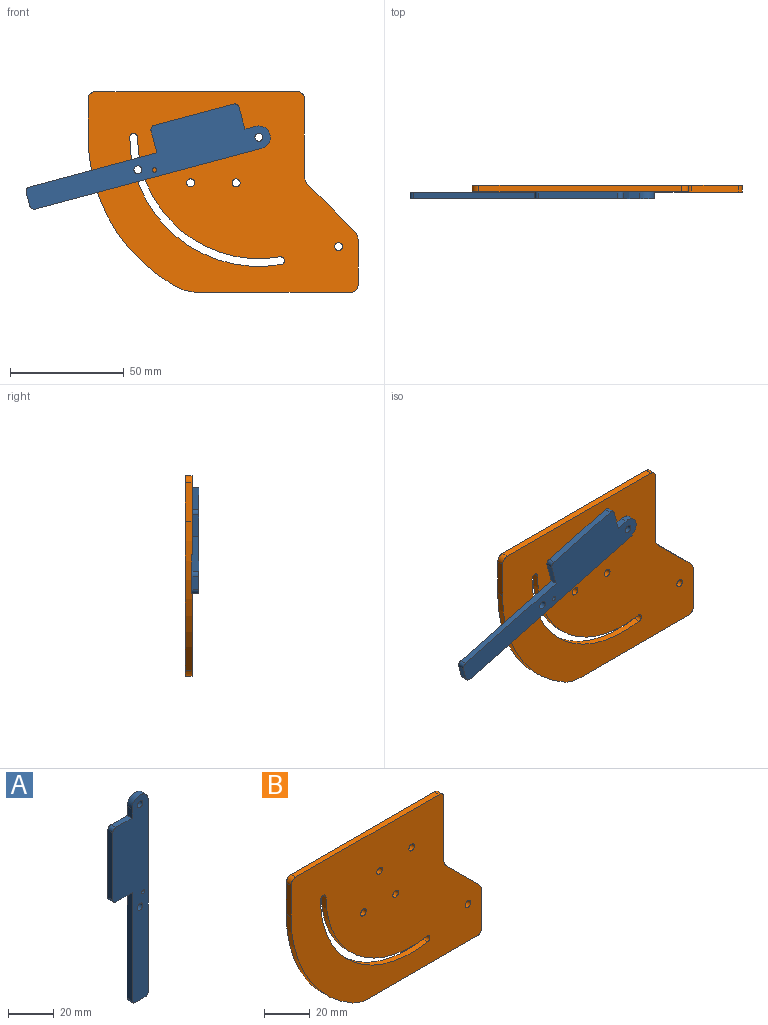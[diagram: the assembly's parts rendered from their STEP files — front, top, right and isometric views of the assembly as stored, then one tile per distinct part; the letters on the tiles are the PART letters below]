
ASSEMBLY  parts=2 mates=1
PART A: 17 faces, bbox 22x3x110 mm
  f0: cylinder r=2mm len=3mm, axis (0,1,0), area 9.4mm2, adj f1,f14,f15,f16
  f1: plane 6x3mm, normal (0,0,-1), area 18mm2, adj f0,f2,f15,f16
  f2: cylinder r=2mm len=3mm, axis (0,1,0), area 9.4mm2, adj f1,f3,f15,f16
  f3: plane 103x3mm, normal (1,0,0), area 309mm2, adj f2,f4,f15,f16
  f4: cylinder r=5mm len=10mm, axis (0,1,0), area 47.1mm2, adj f3,f5,f15,f16
  f5: plane 5x3mm, normal (-1,0,0), area 15mm2, adj f4,f6,f15,f16
  f6: plane 10x3mm, normal (0,0,1), area 30mm2, adj f5,f7,f15,f16
  f7: cylinder r=2mm len=3mm, axis (0,1,0), area 9.4mm2, adj f6,f8,f15,f16
  f8: plane 36x3mm, normal (-1,0,0), area 108mm2, adj f7,f9,f15,f16
  f9: cylinder r=2mm len=3mm, axis (0,1,0), area 9.4mm2, adj f8,f10,f15,f16
  f10: plane 10x3mm, normal (0,0,-1), area 30mm2, adj f9,f14,f15,f16
  f11: cylinder r=1.75mm len=3.5mm, axis (0,1,0), area 33mm2, adj f15,f16
  f12: cylinder r=1.75mm len=3.5mm, axis (0,1,0), area 33mm2, adj f15,f16
  f13: cylinder r=1mm len=3mm, axis (0,1,0), area 18.8mm2, adj f15,f16
  f14: plane 58x3mm, normal (-1,0,0), area 174mm2, adj f0,f10,f15,f16
  f15: plane 110x22mm, normal (0,-1,0), area 1543.5mm2, adj f0,f1,f2,f3,f4,f5,f6,f7
  f16: plane 110x22mm, normal (0,1,0), area 1543.5mm2, adj f0,f1,f2,f3,f4,f5,f6,f7
PART B: 24 faces, bbox 118.5x3x88 mm
  f0: plane 34.17x3mm, normal (1,0,0), area 102.5mm2, adj f1,f21,f22,f23
  f1: cylinder r=3mm len=3mm, axis (0,1,0), area 14.1mm2, adj f0,f2,f22,f23
  f2: plane 89x3mm, normal (0,0,1), area 267mm2, adj f1,f3,f22,f23
  f3: cylinder r=3mm len=3mm, axis (0,1,0), area 14.1mm2, adj f2,f4,f22,f23
  f4: plane 17x3mm, normal (-1,0,0), area 51mm2, adj f3,f5,f22,f23
  f5: cylinder r=75mm len=65.45mm, axis (0,1,0), area 238.7mm2, adj f4,f6,f22,f23
  f6: cylinder r=20mm len=9.76mm, axis (0,1,0), area 30.6mm2, adj f5,f7,f22,f23
  f7: plane 67.36x3mm, normal (0,0,-1), area 202.1mm2, adj f6,f8,f22,f23
  f8: cylinder r=3mm len=3mm, axis (0,1,0), area 14.1mm2, adj f7,f9,f22,f23
  f9: plane 20.18x3mm, normal (1,0,0), area 60.5mm2, adj f8,f10,f22,f23
  f10: cylinder r=5mm len=3.54mm, axis (0,1,0), area 11.8mm2, adj f9,f11,f22,f23
  f11: plane 20.58x20.58mm, normal (0.71,0,0.71), area 87.3mm2, adj f10,f21,f22,f23
  f12: cylinder r=1.7mm len=3.4mm, axis (0,1,0), area 16mm2, adj f13,f20,f22,f23
  f13: cylinder r=53.3mm len=62.56mm, axis (0,1,0), area 279.1mm2, adj f12,f14,f22,f23
  f14: cylinder r=1.7mm len=3.37mm, axis (0,1,0), area 16mm2, adj f13,f20,f22,f23
  f15: cylinder r=1.75mm len=3.5mm, axis (0,1,0), area 33mm2, adj f22,f23
  f16: cylinder r=1.75mm len=3.5mm, axis (0,1,0), area 33mm2, adj f22,f23
  f17: cylinder r=1.75mm len=3.5mm, axis (0,1,0), area 33mm2, adj f22,f23
  f18: cylinder r=1.75mm len=3.5mm, axis (0,1,0), area 33mm2, adj f22,f23
  f19: cylinder r=1.75mm len=3.5mm, axis (0,1,0), area 33mm2, adj f22,f23
  f20: cylinder r=56.7mm len=66.55mm, axis (0,1,0), area 296.9mm2, adj f12,f14,f22,f23
  f21: cylinder r=5mm len=3.54mm, axis (0,1,0), area 11.8mm2, adj f0,f11,f22,f23
  f22: plane 118.51x88mm, normal (0,-1,0), area 8007.6mm2, adj f0,f1,f2,f3,f4,f5,f6,f7
  f23: plane 118.51x88mm, normal (0,1,0), area 8007.6mm2, adj f0,f1,f2,f3,f4,f5,f6,f7
PLACE A rot(axis=(0,1,0),75deg) t=(-118.16,-3,-23.68)mm
PLACE B t=(73.76,0,-22.84)mm
MATE revolute A.f4 <-> B.f5  axis (0,1,0) through (-121.7,-3,-29.81)mm
